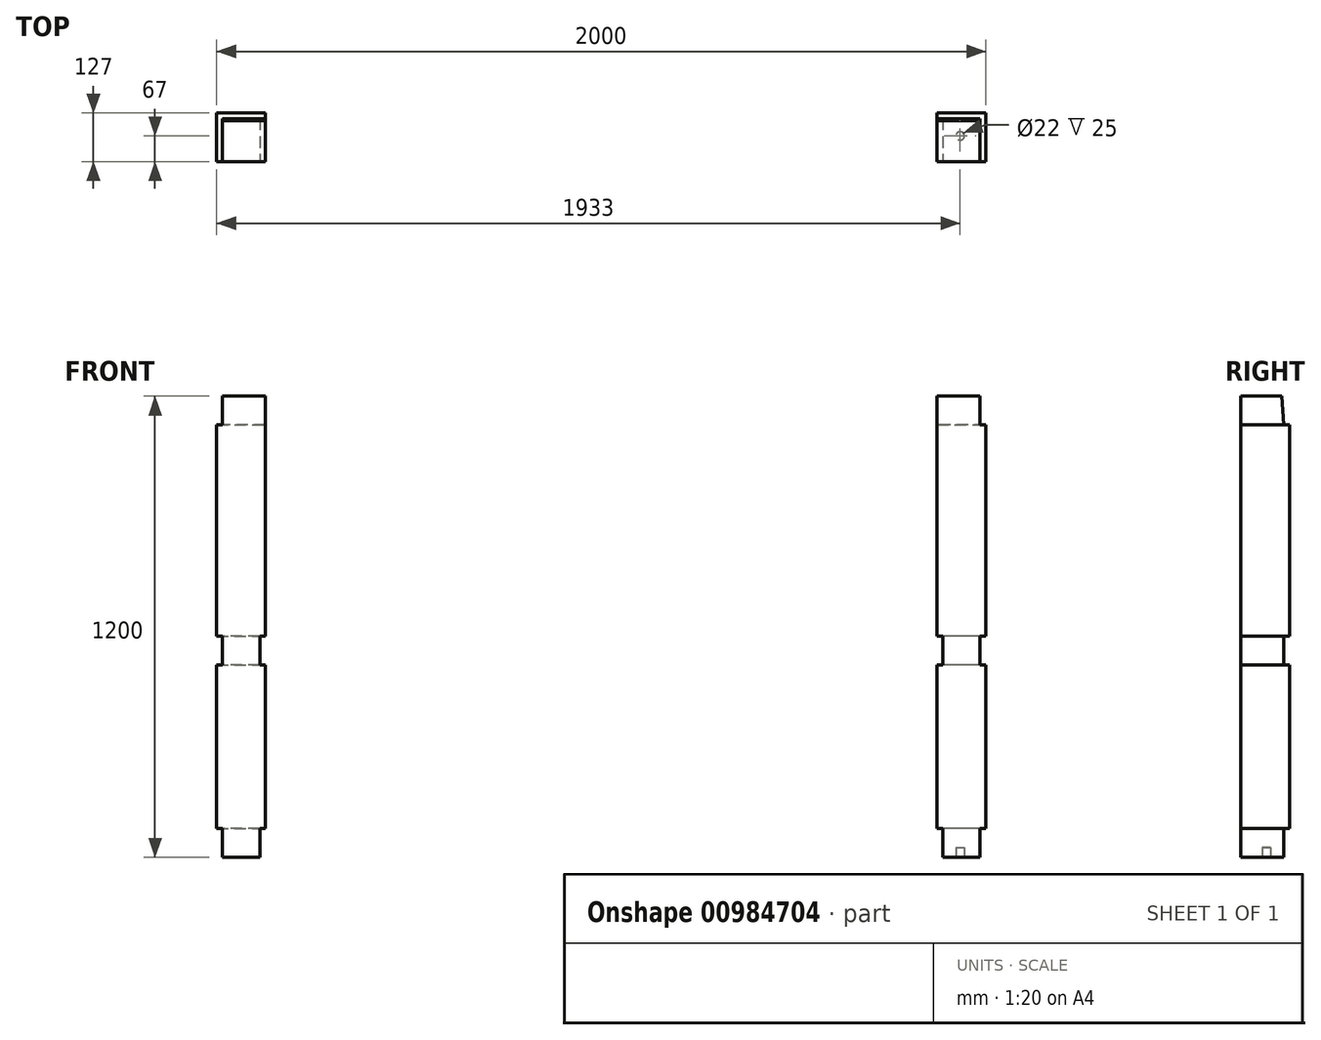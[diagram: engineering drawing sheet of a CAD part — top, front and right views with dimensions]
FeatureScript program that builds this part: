
annotation { "Feature Type Name" : "Feature", "Feature Type Description" : "" }
export const myFeature = defineFeature(function(context is Context, id is Id, definition is map)
    precondition{}
    {
        {
            var Q0;
            Q0=qCreatedBy(makeId("Top.planeOp"),FACE);
            var sketch = newSketch(context, id + "F0", { "sketchPlane" : qUnion([Q0])});
            skLineSegment(sketch, "E0.bottom", {"start": v(0, 0) * mm, "end": v(127, 0) * mm});
            skLineSegment(sketch, "E0.top", {"start": v(0, 127) * mm, "end": v(127, 127) * mm});
            skLineSegment(sketch, "E0.left", {"start": v(0, 0) * mm, "end": v(0, 127) * mm});
            skLineSegment(sketch, "E0.right", {"start": v(127, 0) * mm, "end": v(127, 127) * mm});
            skSolve(sketch);
        }
        {
            var Q0;
            Q0=qSketchRegion(id+"F0",true);
            extrude(context, id + "F1", {"entities" : qUnion([Q0]), "depth" : 1200 * mm, "offsetDistance" : 25.4 * mm});
        }
        {
            var Q0;
            Q0=makeQuery(id+"F1.opExtrude","CAP_FACE",FACE,{"disambiguationData":[OSD([sQuery(id+"F0.wireOp",EDGE,"E0.bottom"),sQuery(id+"F0.wireOp",EDGE,"E0.top"),sQuery(id+"F0.wireOp",EDGE,"E0.left"),sQuery(id+"F0.wireOp",EDGE,"E0.right")])],"isStart":false});
            var sketch = newSketch(context, id + "F2", { "sketchPlane" : qUnion([Q0])});
            skLineSegment(sketch, "E1", {"start": v(0, 0) * mm, "end": v(0, 127) * mm});
            skLineSegment(sketch, "E2", {"start": v(0, 127) * mm, "end": v(127, 127) * mm});
            skLineSegment(sketch, "E3", {"start": v(127, 127) * mm, "end": v(127, 112) * mm});
            skLineSegment(sketch, "E4", {"start": v(127, 112) * mm, "end": v(15, 112) * mm});
            skLineSegment(sketch, "E5", {"start": v(15, 112) * mm, "end": v(15, 0) * mm});
            skLineSegment(sketch, "E6", {"start": v(15, 0) * mm, "end": v(0, 0) * mm});
            skSolve(sketch);
        }
        {
            var Q0;
            Q0=qSketchRegion(id+"F2",true);
            extrude(context, id + "F3", {"entities" : qUnion([Q0]), "operationType" : NewBodyOperationType.REMOVE, "oppositeDirection" : true, "depth" : 75 * mm, "offsetDistance" : 25.4 * mm});
        }
        {
            var Q0;
            Q0=makeQuery(id+"F1.opExtrude","CAP_FACE",FACE,{"disambiguationData":[OSD([sQuery(id+"F0.wireOp",EDGE,"E0.bottom"),sQuery(id+"F0.wireOp",EDGE,"E0.top"),sQuery(id+"F0.wireOp",EDGE,"E0.left"),sQuery(id+"F0.wireOp",EDGE,"E0.right")])],"isStart":true});
            var sketch = newSketch(context, id + "F4", { "sketchPlane" : qUnion([Q0])});
            skLineSegment(sketch, "E7", {"start": v(0, 0) * mm, "end": v(15, 0) * mm});
            skLineSegment(sketch, "E8", {"start": v(0, -127) * mm, "end": v(0, 0) * mm});
            skLineSegment(sketch, "E9", {"start": v(15, 0) * mm, "end": v(15, -127) * mm});
            skLineSegment(sketch, "E10", {"start": v(0, -127) * mm, "end": v(15, -127) * mm});
            skSolve(sketch);
        }
        {
            var Q0;
            Q0=qSketchRegion(id+"F4",true);
            extrude(context, id + "F5", {"entities" : qUnion([Q0]), "operationType" : NewBodyOperationType.REMOVE, "oppositeDirection" : true, "depth" : 575 * mm, "offsetDistance" : 25.4 * mm, "hasSecondDirection" : true, "secondDirectionOppositeDirection" : true, "secondDirectionDepth" : 500 * mm});
        }
        {
            var Q0;
            Q0=makeQuery(id+"F1.opExtrude","SWEPT_FACE",FACE,{"disambiguationData":[OSD([sQuery(id+"F0.wireOp",EDGE,"E0.right")])]});
            var sketch = newSketch(context, id + "F6", { "sketchPlane" : qUnion([Q0])});
            skLineSegment(sketch, "E11", {"start": v(112, 1200) * mm, "end": v(107, 1200) * mm});
            skLineSegment(sketch, "E12", {"start": v(107, 1200) * mm, "end": v(112, 1125) * mm});
            skLineSegment(sketch, "E13", {"start": v(112, 1125) * mm, "end": v(112, 1200) * mm});
            skSolve(sketch);
        }
        {
            var Q0;
            Q0=qSketchRegion(id+"F6",true);
            extrude(context, id + "F7", {"entities" : qUnion([Q0]), "operationType" : NewBodyOperationType.REMOVE, "endBound" : BoundingType.THROUGH_ALL, "oppositeDirection" : true, "depth" : 25.4 * mm, "offsetDistance" : 25.4 * mm});
        }
        {
            var Q0;
            Q0=qCreatedBy(makeId("Right.planeOp"),FACE);
            cPlane(context, id + "F8", {"entities" : qUnion([Q0]), "cplaneType" : CPlaneType.OFFSET, "offset" : 1000 * mm, "width" : 152.4 * mm, "height" : 152.4 * mm});
        }
        {
            var Q0;
            Q0=makeQuery(id+"F1.opExtrude","SWEPT_BODY",BODY,{"disambiguationData":[OSD([sQuery(id+"F0.wireOp",EDGE,"E0.bottom"),sQuery(id+"F0.wireOp",EDGE,"E0.top"),sQuery(id+"F0.wireOp",EDGE,"E0.left"),sQuery(id+"F0.wireOp",EDGE,"E0.right")])]});
            var Q1;
            Q1=qCreatedBy(id+"F8.planeOp",FACE);
            mirror(context, id + "F9", {"entities" : qUnion([Q0]), "mirrorPlane" : qUnion([Q1])});
        }
        {
            var Q0;
            Q0=makeQuery(id+"F9.opPattern","COPY",FACE,{"derivedFrom":makeQuery(id+"F1.opExtrude","CAP_FACE",FACE,{"disambiguationData":[OSD([sQuery(id+"F0.wireOp",EDGE,"E0.bottom"),sQuery(id+"F0.wireOp",EDGE,"E0.top"),sQuery(id+"F0.wireOp",EDGE,"E0.left"),sQuery(id+"F0.wireOp",EDGE,"E0.right")])],"isStart":true}),"instanceName":"1"});
            var sketch = newSketch(context, id + "F10", { "sketchPlane" : qUnion([Q0])});
            skLineSegment(sketch, "E14", {"start": v(2000, -127) * mm, "end": v(2000, 0) * mm});
            skLineSegment(sketch, "E15", {"start": v(2000, 0) * mm, "end": v(1873, 0) * mm});
            skLineSegment(sketch, "E16", {"start": v(1873, 0) * mm, "end": v(1873, -127) * mm});
            skPoint(sketch, "E17.start.orphan", {"position": v(1985, -127) * mm});
            skLineSegment(sketch, "E18", {"start": v(2000, -127) * mm, "end": v(1873, -127) * mm});
            skLineSegment(sketch, "E19", {"start": v(2000, 0) * mm, "end": v(1985, 0) * mm});
            skLineSegment(sketch, "E20", {"start": v(1985, 0) * mm, "end": v(1985, -112) * mm});
            skLineSegment(sketch, "E21", {"start": v(1985, -112) * mm, "end": v(1888, -112) * mm});
            skLineSegment(sketch, "E22", {"start": v(1888, -112) * mm, "end": v(1888, 0) * mm});
            skLineSegment(sketch, "E23", {"start": v(1888, 0) * mm, "end": v(1873, 0) * mm});
            skSolve(sketch);
        }
        {
            var Q0;
            Q0=makeQuery(id+"F10.imprint","IMPRINT",FACE,{"disambiguationData":[TD([[makeQuery(id+"F10.imprint","IMPRINT",EDGE,{"derivedFrom":sQuery(id+"F10.wireOp",EDGE,"E14")}),-1.0]])]});
            extrude(context, id + "F11", {"entities" : qUnion([Q0]), "operationType" : NewBodyOperationType.REMOVE, "oppositeDirection" : true, "depth" : 75 * mm, "offsetDistance" : 25.4 * mm});
        }
        {
            var Q0;
            Q0=makeQuery(id+"F1.opExtrude","CAP_FACE",FACE,{"disambiguationData":[OSD([sQuery(id+"F0.wireOp",EDGE,"E0.bottom"),sQuery(id+"F0.wireOp",EDGE,"E0.top"),sQuery(id+"F0.wireOp",EDGE,"E0.left"),sQuery(id+"F0.wireOp",EDGE,"E0.right")])],"isStart":true});
            var sketch = newSketch(context, id + "F12", { "sketchPlane" : qUnion([Q0])});
            skLineSegment(sketch, "E24", {"start": v(127, -127) * mm, "end": v(127, 0) * mm});
            skLineSegment(sketch, "E25", {"start": v(0, 0) * mm, "end": v(0, -127) * mm});
            skPoint(sketch, "E26.start.orphan", {"position": v(112, -127) * mm});
            skLineSegment(sketch, "E27", {"start": v(127, 0) * mm, "end": v(112, 0) * mm});
            skLineSegment(sketch, "E28", {"start": v(112, 0) * mm, "end": v(112, -112) * mm});
            skLineSegment(sketch, "E29", {"start": v(112, -112) * mm, "end": v(15, -112) * mm});
            skLineSegment(sketch, "E30", {"start": v(15, -112) * mm, "end": v(15, 0) * mm});
            skLineSegment(sketch, "E31", {"start": v(15, 0) * mm, "end": v(0, 0) * mm});
            skLineSegment(sketch, "E32", {"start": v(127, -127) * mm, "end": v(0, -127) * mm});
            skSolve(sketch);
        }
        {
            var Q0;
            Q0=makeQuery(id+"F12.imprint","IMPRINT",FACE,{"disambiguationData":[TD([[makeQuery(id+"F12.imprint","IMPRINT",EDGE,{"derivedFrom":sQuery(id+"F12.wireOp",EDGE,"h6Yfyvmf-z5Va-JGNE-2V0m-nFTmjVJeydvc")}),1.0]])]});
            var Q1;
            Q1=makeQuery(id+"F12.imprint","IMPRINT",FACE,{"disambiguationData":[TD([[makeQuery(id+"F12.imprint","IMPRINT",EDGE,{"derivedFrom":sQuery(id+"F12.wireOp",EDGE,"E24")}),-1.0]])]});
            extrude(context, id + "F13", {"entities" : qUnion([Q0, Q1]), "operationType" : NewBodyOperationType.REMOVE, "oppositeDirection" : true, "depth" : 75 * mm, "offsetDistance" : 25.4 * mm});
        }
        {
            var Q0;
            Q0=makeQuery(id+"F1.opExtrude","SWEPT_FACE",FACE,{"disambiguationData":[OSD([sQuery(id+"F0.wireOp",EDGE,"E0.bottom")])]});
            var sketch = newSketch(context, id + "F14", { "sketchPlane" : qUnion([Q0])});
            skLineSegment(sketch, "E33.bottom", {"start": v(127, 575) * mm, "end": v(112, 575) * mm});
            skLineSegment(sketch, "E33.top", {"start": v(127, 500) * mm, "end": v(112, 500) * mm});
            skLineSegment(sketch, "E33.left", {"start": v(127, 575) * mm, "end": v(127, 500) * mm});
            skLineSegment(sketch, "E33.right", {"start": v(112, 575) * mm, "end": v(112, 500) * mm});
            skSolve(sketch);
        }
        {
            var Q0;
            Q0=makeQuery(id+"F14.imprint","IMPRINT",FACE,{"disambiguationData":[TD([[makeQuery(id+"F14.imprint","IMPRINT",EDGE,{"derivedFrom":sQuery(id+"F14.wireOp",EDGE,"E33.bottom")}),1.0]])]});
            extrude(context, id + "F15", {"entities" : qUnion([Q0]), "operationType" : NewBodyOperationType.REMOVE, "endBound" : BoundingType.THROUGH_ALL, "oppositeDirection" : true, "depth" : 25 * mm, "offsetDistance" : 25 * mm});
        }
        {
            var Q0;
            Q0=makeQuery(id+"F9.opPattern","COPY",FACE,{"derivedFrom":makeQuery(id+"F1.opExtrude","SWEPT_FACE",FACE,{"disambiguationData":[OSD([sQuery(id+"F0.wireOp",EDGE,"E0.bottom")])]}),"instanceName":"1"});
            var sketch = newSketch(context, id + "F16", { "sketchPlane" : qUnion([Q0])});
            skLineSegment(sketch, "E34.bottom", {"start": v(1873, 575) * mm, "end": v(1888, 575) * mm});
            skLineSegment(sketch, "E34.top", {"start": v(1873, 500) * mm, "end": v(1888, 500) * mm});
            skLineSegment(sketch, "E34.left", {"start": v(1873, 575) * mm, "end": v(1873, 500) * mm});
            skLineSegment(sketch, "E34.right", {"start": v(1888, 575) * mm, "end": v(1888, 500) * mm});
            skSolve(sketch);
        }
        {
            var Q0;
            Q0=makeQuery(id+"F16.imprint","IMPRINT",FACE,{"disambiguationData":[TD([[makeQuery(id+"F16.imprint","IMPRINT",EDGE,{"derivedFrom":sQuery(id+"F16.wireOp",EDGE,"E34.bottom")}),-1.0]])]});
            extrude(context, id + "F17", {"entities" : qUnion([Q0]), "operationType" : NewBodyOperationType.REMOVE, "endBound" : BoundingType.THROUGH_ALL, "oppositeDirection" : true, "depth" : 25 * mm, "offsetDistance" : 25 * mm});
        }
        {
            var Q0;
            Q0=makeQuery(id+"F5.boolean.opBoolean","COPY",FACE,{"derivedFrom":makeQuery(id+"F5.opExtrude","SWEPT_FACE",FACE,{"disambiguationData":[OSD([sQuery(id+"F4.wireOp",EDGE,"E9")])]})});
            var sketch = newSketch(context, id + "F18", { "sketchPlane" : qUnion([Q0])});
            skLineSegment(sketch, "E35.bottom", {"start": v(-127, 575) * mm, "end": v(-112, 575) * mm});
            skLineSegment(sketch, "E35.top", {"start": v(-127, 500) * mm, "end": v(-112, 500) * mm});
            skLineSegment(sketch, "E35.left", {"start": v(-127, 575) * mm, "end": v(-127, 500) * mm});
            skLineSegment(sketch, "E35.right", {"start": v(-112, 575) * mm, "end": v(-112, 500) * mm});
            skSolve(sketch);
        }
        {
            var Q0;
            Q0=makeQuery(id+"F18.imprint","IMPRINT",FACE,{"disambiguationData":[TD([[makeQuery(id+"F18.imprint","IMPRINT",EDGE,{"derivedFrom":sQuery(id+"F18.wireOp",EDGE,"E35.bottom")}),1.0]])]});
            extrude(context, id + "F19", {"entities" : qUnion([Q0]), "operationType" : NewBodyOperationType.REMOVE, "endBound" : BoundingType.THROUGH_ALL, "oppositeDirection" : true, "depth" : 25 * mm, "offsetDistance" : 25 * mm});
        }
        {
            var Q0;
            Q0=makeQuery(id+"F17.boolean.opBoolean","COPY",FACE,{"derivedFrom":makeQuery(id+"F17.opExtrude","SWEPT_FACE",FACE,{"disambiguationData":[OSD([sQuery(id+"F16.wireOp",EDGE,"E34.right")])]})});
            var sketch = newSketch(context, id + "F20", { "sketchPlane" : qUnion([Q0])});
            skLineSegment(sketch, "E36.bottom", {"start": v(-127, 575) * mm, "end": v(-112, 575) * mm});
            skLineSegment(sketch, "E36.top", {"start": v(-127, 500) * mm, "end": v(-112, 500) * mm});
            skLineSegment(sketch, "E36.left", {"start": v(-127, 575) * mm, "end": v(-127, 500) * mm});
            skLineSegment(sketch, "E36.right", {"start": v(-112, 575) * mm, "end": v(-112, 500) * mm});
            skSolve(sketch);
        }
        {
            var Q0;
            Q0 = qSketchRegion(id + "F20", true);
            extrude(context, id + "F21", {"entities" : qUnion([Q0]), "operationType" : NewBodyOperationType.REMOVE, "endBound" : BoundingType.THROUGH_ALL, "oppositeDirection" : true, "depth" : 25 * mm, "offsetDistance" : 25 * mm});
        }
        {
            var Q0;
            Q0=makeQuery(id+"F9.opPattern","COPY",FACE,{"derivedFrom":makeQuery(id+"F1.opExtrude","CAP_FACE",FACE,{"disambiguationData":[OSD([sQuery(id+"F0.wireOp",EDGE,"E0.bottom"),sQuery(id+"F0.wireOp",EDGE,"E0.top"),sQuery(id+"F0.wireOp",EDGE,"E0.left"),sQuery(id+"F0.wireOp",EDGE,"E0.right")])],"isStart":true}),"instanceName":"1"});
            var sketch = newSketch(context, id + "F22", { "sketchPlane" : qUnion([Q0])});
            skCircle(sketch, "E37", {"center": v(1933, -67) * mm, "radius": 11 * mm});
            skSolve(sketch);
        }
        {
            var Q0;
            Q0=makeQuery(id+"F22.imprint","IMPRINT",FACE,{"disambiguationData":[TD([[makeQuery(id+"F22.imprint","IMPRINT",EDGE,{"derivedFrom":sQuery(id+"F22.wireOp",EDGE,"E37")}),1.0]])]});
            extrude(context, id + "F23", {"entities" : qUnion([Q0]), "operationType" : NewBodyOperationType.REMOVE, "oppositeDirection" : true, "depth" : 25 * mm, "offsetDistance" : 25 * mm});
        }
    });
